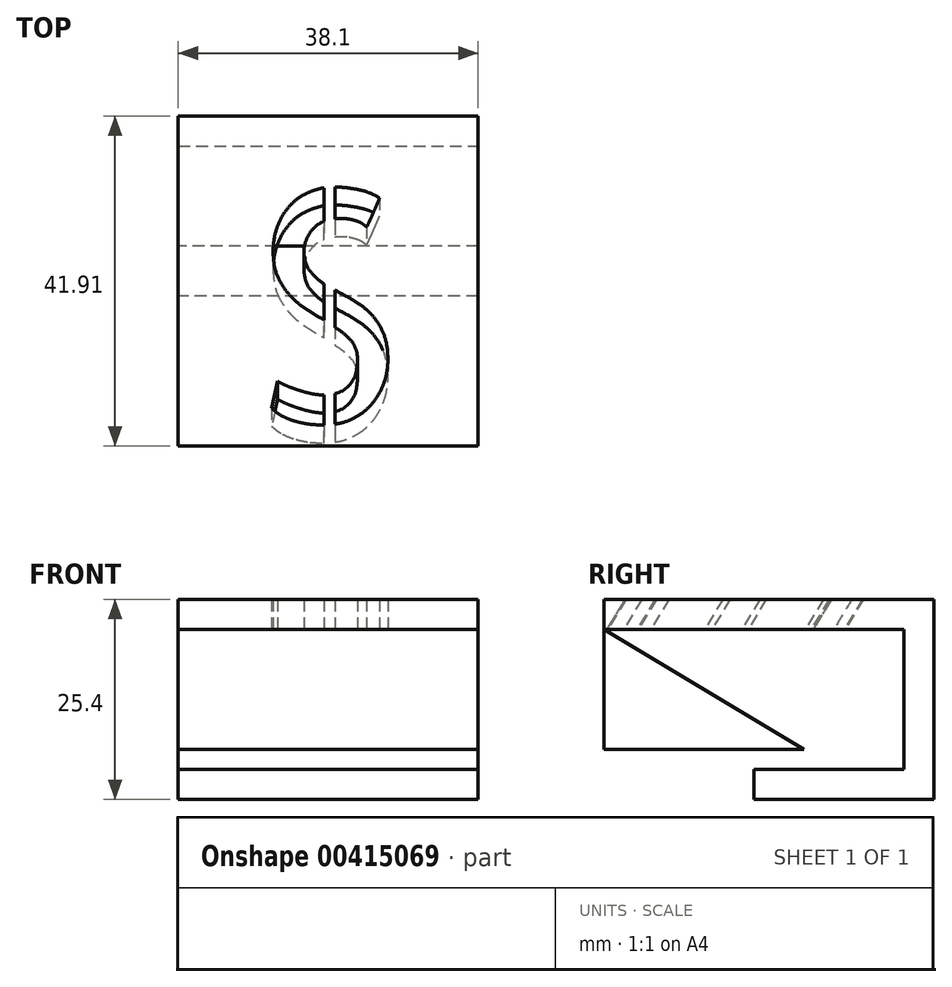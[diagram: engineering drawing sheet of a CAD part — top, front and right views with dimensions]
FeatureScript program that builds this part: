
annotation { "Feature Type Name" : "Feature", "Feature Type Description" : "" }
export const myFeature = defineFeature(function(context is Context, id is Id, definition is map)
    precondition{}
    {
        {
            var Q0;
            Q0=qCreatedBy(makeId("Top.planeOp"),FACE);
            var sketch = newSketch(context, id + "F0", { "sketchPlane" : qUnion([Q0])});
            skLineSegment(sketch, "E0.bottom", {"start": v(0, 0) * mm, "end": v(38.1, 0) * mm});
            skLineSegment(sketch, "E0.top", {"start": v(0, 38.1) * mm, "end": v(38.1, 38.1) * mm});
            skLineSegment(sketch, "E0.left", {"start": v(0, 0) * mm, "end": v(0, 38.1) * mm});
            skLineSegment(sketch, "E0.right", {"start": v(38.1, 0) * mm, "end": v(38.1, 38.1) * mm});
            skSolve(sketch);
        }
        {
            var Q0;
            Q0=makeQuery(id+"F0.imprint","IMPRINT",FACE,{"disambiguationData":[TD([[makeQuery(id+"F0.imprint","IMPRINT",EDGE,{"derivedFrom":sQuery(id+"F0.wireOp",EDGE,"E0.bottom")}),1.0]])]});
            extrude(context, id + "F1", {"entities" : qUnion([Q0]), "depth" : 3.8 * mm});
        }
        {
            var Q0;
            Q0=qCreatedBy(makeId("Right.planeOp"),FACE);
            var sketch = newSketch(context, id + "F2", { "sketchPlane" : qUnion([Q0])});
            skLineSegment(sketch, "E1", {"start": v(0, 0) * mm, "end": v(25.4, -15.24) * mm});
            skLineSegment(sketch, "E2", {"start": v(25.4, -15.24) * mm, "end": v(0, -15.24) * mm});
            skLineSegment(sketch, "E3", {"start": v(0, -15.24) * mm, "end": v(0, 0) * mm});
            skSolve(sketch);
        }
        {
            var Q0;
            Q0 = qSketchRegion(id + "F2", true);
            extrude(context, id + "F3", {"entities" : qUnion([Q0]), "depth" : 38.1 * mm});
        }
        {
            var Q0;
            Q0=makeQuery(id+"F3.opExtrude","SWEPT_FACE",FACE,{"disambiguationData":[OSD([sQuery(id+"F2.wireOp",EDGE,"E1")])]});
            var sketch = newSketch(context, id + "F4", { "sketchPlane" : qUnion([Q0])});
            skText(sketch, "E4", { "text": "S", "fontName": "AllertaStencil-Regular.ttf"});
            const initialGuessF4  = {"E4": [0.0091, 0.00046, 1, 0, 0.0254]};
            skSetInitialGuess(sketch, initialGuessF4);
            skSolve(sketch);
        }
        {
            var Q0;
            Q0 = qSketchRegion(id + "F4", true);
            extrude(context, id + "F5", {"entities" : qUnion([Q0]), "operationType" : NewBodyOperationType.REMOVE, "depth" : 25.4 * mm});
        }
        {
            var Q0;
            Q0=makeQuery(id+"F1.opExtrude","CAP_FACE",FACE,{"disambiguationData":[OSD([sQuery(id+"F0.wireOp",EDGE,"E0.bottom"),sQuery(id+"F0.wireOp",EDGE,"E0.top"),sQuery(id+"F0.wireOp",EDGE,"E0.left"),sQuery(id+"F0.wireOp",EDGE,"E0.right")])],"isStart":false});
            var sketch = newSketch(context, id + "F6", { "sketchPlane" : qUnion([Q0])});
            skLineSegment(sketch, "E5.bottom", {"start": v(38.1, 38.1) * mm, "end": v(0, 38.1) * mm});
            skLineSegment(sketch, "E5.top", {"start": v(38.1, 41.9) * mm, "end": v(0, 41.9) * mm});
            skLineSegment(sketch, "E5.left", {"start": v(38.1, 38.1) * mm, "end": v(38.1, 41.9) * mm});
            skLineSegment(sketch, "E5.right", {"start": v(0, 38.1) * mm, "end": v(0, 41.9) * mm});
            skSolve(sketch);
        }
        {
            var Q0;
            Q0 = qSketchRegion(id + "F6", true);
            extrude(context, id + "F7", {"entities" : qUnion([Q0]), "operationType" : NewBodyOperationType.ADD, "oppositeDirection" : true, "depth" : 25.4 * mm});
        }
        {
            var Q0;
            Q0=makeQuery(id+"F7.boolean.opBoolean","MERGE",FACE,{"derivedFrom":[makeQuery(id+"F1.opExtrude","SWEPT_FACE",FACE,{"disambiguationData":[OSD([sQuery(id+"F0.wireOp",EDGE,"E0.left")])]}),makeQuery(id+"F7.opExtrude","SWEPT_FACE",FACE,{"disambiguationData":[OSD([sQuery(id+"F6.wireOp",EDGE,"E5.right")])]})]});
            var sketch = newSketch(context, id + "F8", { "sketchPlane" : qUnion([Q0])});
            skLineSegment(sketch, "E6", {"start": v(-38.1, -21.59) * mm, "end": v(-19.05, -21.59) * mm});
            skLineSegment(sketch, "E7.0", {"start": v(-38.1, -17.78) * mm, "end": v(-19.05, -17.78) * mm});
            skLineSegment(sketch, "E8", {"start": v(-19.05, -17.78) * mm, "end": v(-19.05, -21.59) * mm});
            skLineSegment(sketch, "E9", {"start": v(-38.1, -21.59) * mm, "end": v(-38.1, -17.78) * mm});
            skSolve(sketch);
        }
        {
            var Q0;
            Q0=makeQuery(id+"F8.imprint","IMPRINT",FACE,{"disambiguationData":[TD([[makeQuery(id+"F8.imprint","IMPRINT",EDGE,{"derivedFrom":sQuery(id+"F8.wireOp",EDGE,"E6")}),1.0]])]});
            extrude(context, id + "F9", {"entities" : qUnion([Q0]), "operationType" : NewBodyOperationType.ADD, "oppositeDirection" : true, "depth" : 38.1 * mm});
        }
    });
